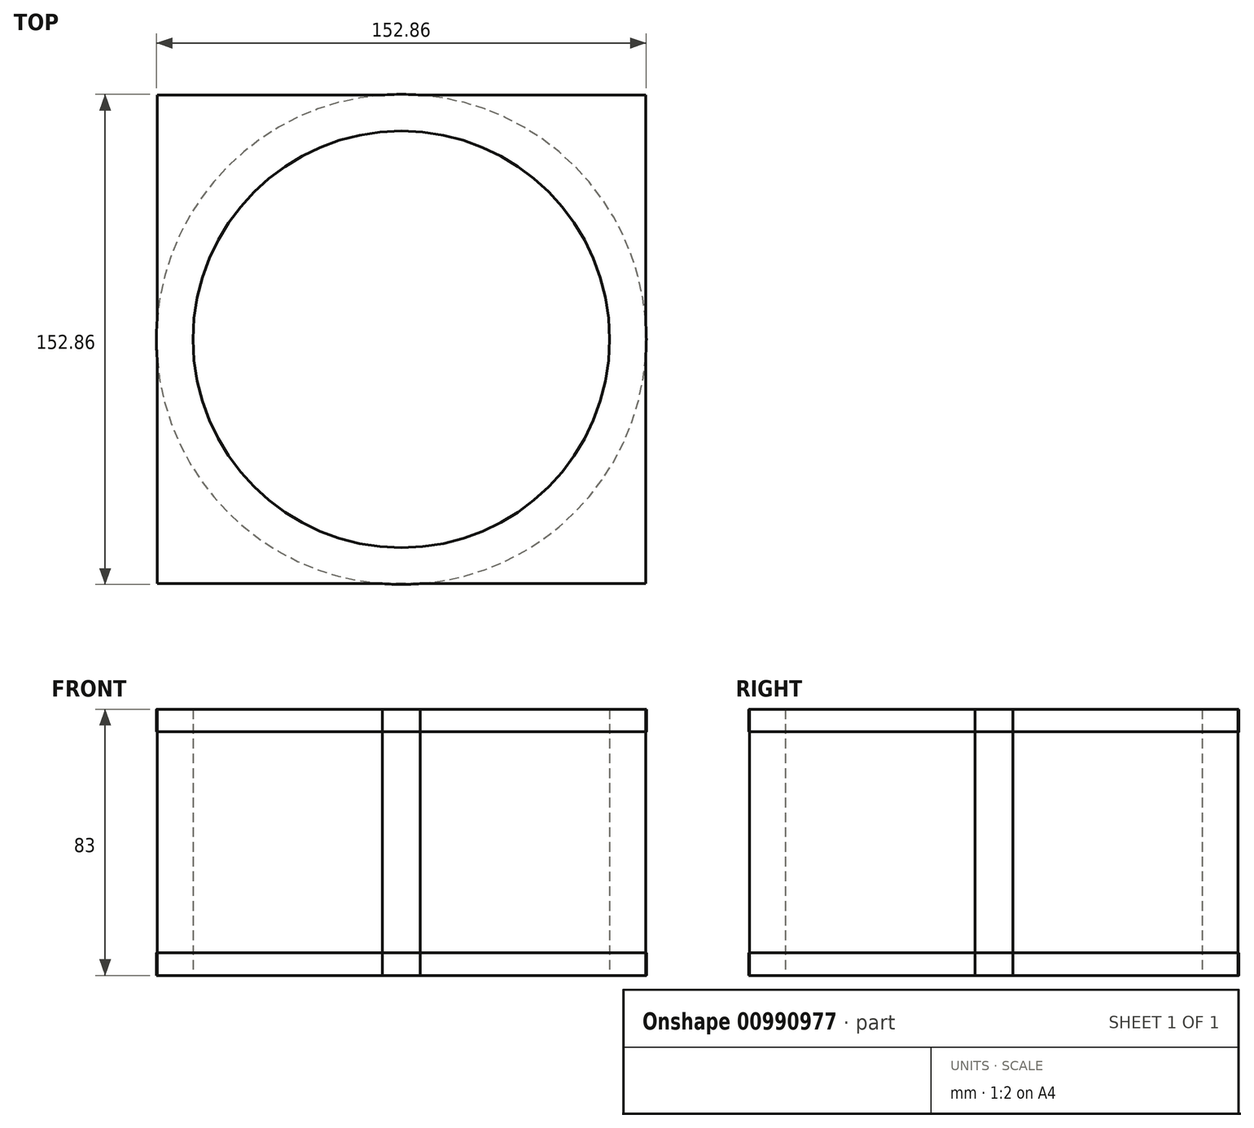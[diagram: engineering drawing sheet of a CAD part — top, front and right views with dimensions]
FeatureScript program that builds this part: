
annotation { "Feature Type Name" : "Feature", "Feature Type Description" : "" }
export const myFeature = defineFeature(function(context is Context, id is Id, definition is map)
    precondition{}
    {
        {
            var Q0;
            Q0=qCreatedBy(makeId("Top.planeOp"),FACE);
            var sketch = newSketch(context, id + "F0", { "sketchPlane" : qUnion([Q0])});
            skCircle(sketch, "E0", {"center": v(0, 0) * mm, "radius": 65 * mm});
            skLineSegment(sketch, "E1.bottom", {"start": v(76.2, -76.2) * mm, "end": v(-76.2, -76.2) * mm});
            skLineSegment(sketch, "E1.top", {"start": v(76.2, 76.2) * mm, "end": v(-76.2, 76.2) * mm});
            skLineSegment(sketch, "E1.left", {"start": v(76.2, -76.2) * mm, "end": v(76.2, 76.2) * mm});
            skLineSegment(sketch, "E1.right", {"start": v(-76.2, -76.2) * mm, "end": v(-76.2, 76.2) * mm});
            skPoint(sketch, "E2", {"position": v(-76.2, 0) * mm});
            skPoint(sketch, "E3", {"position": v(76.2, 0) * mm});
            skPoint(sketch, "E4", {"position": v(0, 76.2) * mm});
            skPoint(sketch, "E5", {"position": v(0, -76.2) * mm});
            skCircle(sketch, "E6", {"center": v(0, 0) * mm, "radius": 76.43 * mm});
            skSolve(sketch);
        }
        {
            var Q0;
            Q0=makeQuery(id+"F0.imprint","IMPRINT",FACE,{"disambiguationData":[TD([[makeQuery(id+"F0.imprint","IMPRINT",EDGE,{"derivedFrom":sQuery(id+"F0.wireOp",EDGE,"E0")}),-1.0]])]});
            extrude(context, id + "F1", {"entities" : qUnion([Q0]), "depth" : 69 * mm, "offsetDistance" : 25 * mm});
        }
        {
            var Q0;
            Q0 = qSketchRegion(id + "F0", true);
            extrude(context, id + "F2", {"entities" : qUnion([Q0]), "operationType" : NewBodyOperationType.ADD, "oppositeDirection" : true, "depth" : 7 * mm, "offsetDistance" : 25 * mm});
        }
        {
            var Q0;
            Q0=makeQuery(id+"F1.opExtrude","CAP_FACE",FACE,{"disambiguationData":[OSD([sQuery(id+"F0.wireOp",EDGE,"E0"),sQuery(id+"F0.wireOp",EDGE,"E1.bottom"),sQuery(id+"F0.wireOp",EDGE,"E1.top"),sQuery(id+"F0.wireOp",EDGE,"E1.left"),sQuery(id+"F0.wireOp",EDGE,"E1.right"),sQuery(id+"F0.wireOp",EDGE,"E6")])],"isStart":false});
            var sketch = newSketch(context, id + "F3", { "sketchPlane" : qUnion([Q0])});
            skCircle(sketch, "E7", {"center": v(0, 0) * mm, "radius": 65 * mm});
            skLineSegment(sketch, "E8.bottom", {"start": v(76.2, -76.2) * mm, "end": v(-76.2, -76.2) * mm});
            skLineSegment(sketch, "E8.top", {"start": v(76.2, 76.2) * mm, "end": v(-76.2, 76.2) * mm});
            skLineSegment(sketch, "E8.left", {"start": v(76.2, -76.2) * mm, "end": v(76.2, 76.2) * mm});
            skLineSegment(sketch, "E8.right", {"start": v(-76.2, -76.2) * mm, "end": v(-76.2, 76.2) * mm});
            skPoint(sketch, "E9", {"position": v(-76.2, 0) * mm});
            skPoint(sketch, "E10", {"position": v(76.2, 0) * mm});
            skPoint(sketch, "E11", {"position": v(0, 76.2) * mm});
            skPoint(sketch, "E12", {"position": v(0, -76.2) * mm});
            skCircle(sketch, "E13", {"center": v(0, 0) * mm, "radius": 76.43 * mm});
            skSolve(sketch);
        }
        {
            var Q0;
            Q0 = qSketchRegion(id + "F3", true);
            extrude(context, id + "F4", {"entities" : qUnion([Q0]), "operationType" : NewBodyOperationType.ADD, "depth" : 7 * mm, "offsetDistance" : 25 * mm});
        }
    });
